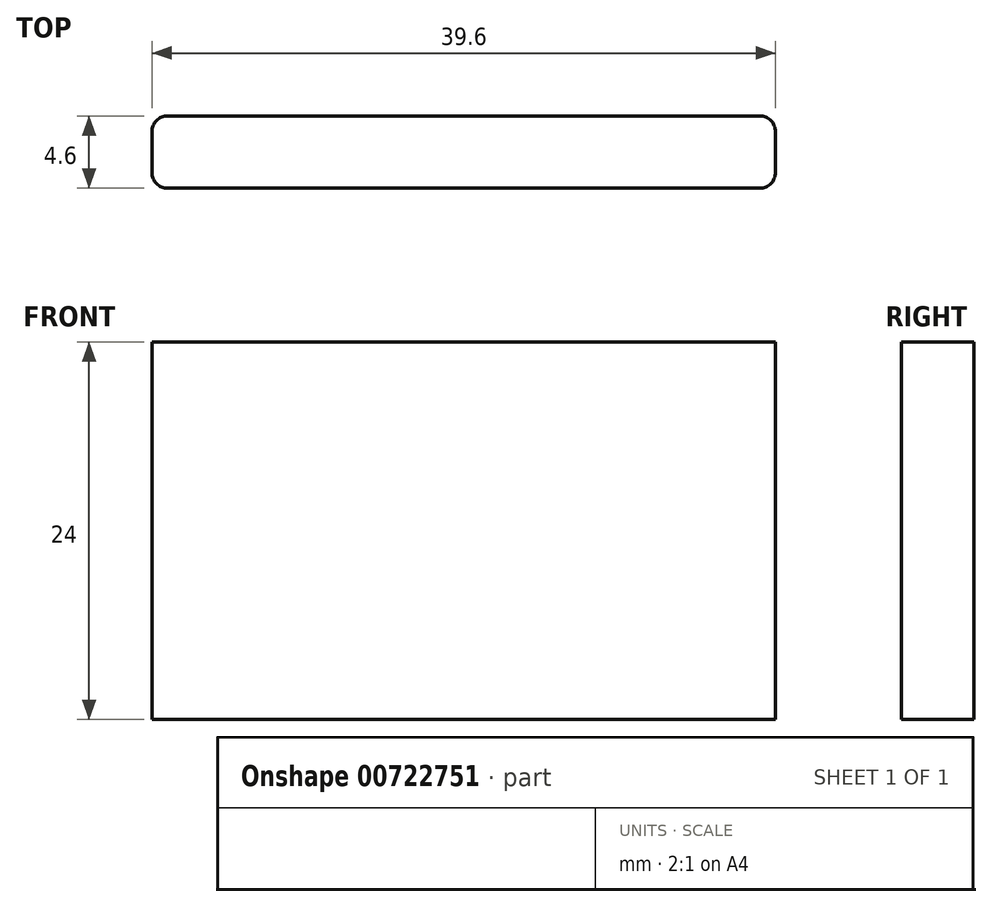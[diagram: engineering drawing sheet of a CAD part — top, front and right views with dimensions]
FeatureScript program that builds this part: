
annotation { "Feature Type Name" : "Feature", "Feature Type Description" : "" }
export const myFeature = defineFeature(function(context is Context, id is Id, definition is map)
    precondition{}
    {
        {
            var Q0;
            Q0=qCreatedBy(makeId("Top.planeOp"),FACE);
            var sketch = newSketch(context, id + "F0", { "sketchPlane" : qUnion([Q0])});
            skLineSegment(sketch, "E0.bottom", {"start": v(-19.8, 2.3) * mm, "end": v(19.8, 2.3) * mm});
            skLineSegment(sketch, "E0.top", {"start": v(-19.8, -2.3) * mm, "end": v(19.8, -2.3) * mm});
            skLineSegment(sketch, "E0.left", {"start": v(-19.8, 2.3) * mm, "end": v(-19.8, -2.3) * mm});
            skLineSegment(sketch, "E0.right", {"start": v(19.8, 2.3) * mm, "end": v(19.8, -2.3) * mm});
            skPoint(sketch, "E0.middle", {"position": v(0, 0) * mm});
            skSolve(sketch);
        }
        {
            var Q0;
            Q0=qSketchRegion(id+"F0",true);
            extrude(context, id + "F1", {"entities" : qUnion([Q0]), "flatOperationType" : FlatOperationType.REMOVE, "depth" : 24 * mm, "offsetDistance" : 25 * mm, "domain" : OperationDomain.MODEL});
        }
        {
            var Q0;
            Q0=makeQuery(id+"F1.opExtrude","SWEPT_EDGE",EDGE,{"disambiguationData":[OSD([sQuery(id+"F0.wireOp",EDGE,"E0.bottom"),sQuery(id+"F0.wireOp",EDGE,"E0.left")])]});
            var Q1;
            Q1=makeQuery(id+"F1.opExtrude","SWEPT_EDGE",EDGE,{"disambiguationData":[OSD([sQuery(id+"F0.wireOp",EDGE,"E0.bottom"),sQuery(id+"F0.wireOp",EDGE,"E0.right")])]});
            var Q2;
            Q2=makeQuery(id+"F1.opExtrude","SWEPT_EDGE",EDGE,{"disambiguationData":[OSD([sQuery(id+"F0.wireOp",EDGE,"E0.top"),sQuery(id+"F0.wireOp",EDGE,"E0.right")])]});
            var Q3;
            Q3=makeQuery(id+"F1.opExtrude","SWEPT_EDGE",EDGE,{"disambiguationData":[OSD([sQuery(id+"F0.wireOp",EDGE,"E0.top"),sQuery(id+"F0.wireOp",EDGE,"E0.left")])]});
            fillet(context, id + "F2", {"entities" : qUnion([Q0, Q1, Q2, Q3]), "radius" : 1 * mm, "tangentPropagation" : true, "allowEdgeOverflow" : false});
        }
    });
